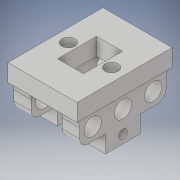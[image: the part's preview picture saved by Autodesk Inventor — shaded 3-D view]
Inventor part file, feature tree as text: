
AUTODESK INVENTOR PART (.ipt)
format: ipt  version: 2019 (Build 230136000, 136)  size: 233,472 bytes
history: native  units: mm
features: extrude x8, sketch x8, fillet x2, hole x1
ambient origin geometry x8: Origin, YZ Plane, XZ Plane, XY Plane, X Axis, Y Axis, Z Axis, Center Point
bodies: Solid1 (feature_tree)
feature tree (19):
  extrude  "Extrusion1"  Depth=80.0mm
  extrude  "Extrusion2"  Depth=30.0mm
  hole  "Hole1"  [1 undecoded]
  extrude  "Extrusion3"  Depth=20.0mm
  fillet  "Fillet1"  Radius=2.0mm
  fillet  "Fillet3"  Radius=30.0mm
  extrude  "Extrusion4"  Depth=15.0mm
  sketch  "Sketch6"  dims[d20=15.0mm d21=25.0mm]
  extrude  "Extrusion6"  Depth=25.0mm
  extrude  "Extrusion7"  Depth=15.0mm TaperAngle=0.0deg
  extrude  "Extrusion8"  Depth=10.0mm
  extrude  "Extrusion9"  Depth=45.0mm
  sketch  "Sketch1"  dims[d0=110.0mm d1=80.0mm]
  sketch  "Sketch2"  dims[d2=20.0mm d3=0.0mm d4=30.0mm]
  sketch  "Sketch3"  dims[d5=20.0mm d6=20.0mm]
  sketch  "Sketch4"  dims[d7=2.0mm d8=20.0mm d9=2.0mm d10=30.0mm d11=0.0mm]
  sketch  "Sketch5"  dims[d12=20.0mm d13=6.0mm d14=4.0mm d15=2.0mm d16=90.0deg d17=15.0mm d18=20.594885mm d19=15.0mm]
  sketch  "Sketch7"  dims[d23=25.0mm d24=15.0mm d25=0.0mm]
  sketch  "Sketch9"  dims[d26=10.0mm d28=10.0mm d30=45.0mm d31=30.0mm d32=20.0mm d33=0.0mm d37=50.0mm d38=0.0mm d39=50.0mm d40=0.0mm d42=20.0mm d43=15.0mm d44=100.0mm d45=0.0mm d46=10.0mm d47=10.0mm d48=100.0mm d49=0.0mm d22=0.75mm]
note: 1 required parameter value undecoded (feature->parameter linkage not recoverable at this tier; creation-order binding heuristic only, values carry confidence <= 0.55)
